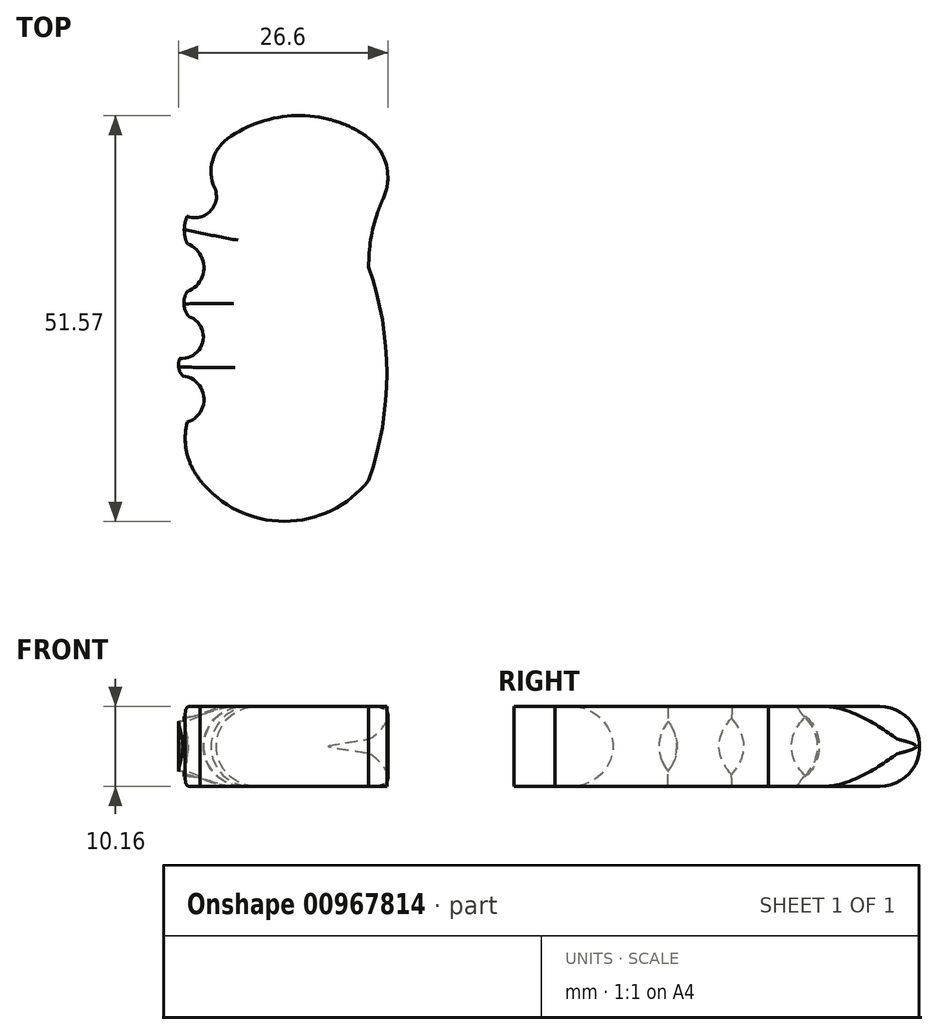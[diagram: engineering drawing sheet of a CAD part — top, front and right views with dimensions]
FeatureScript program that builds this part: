
annotation { "Feature Type Name" : "Feature", "Feature Type Description" : "" }
export const myFeature = defineFeature(function(context is Context, id is Id, definition is map)
    precondition{}
    {
        {
            var Q0;
            Q0=qCreatedBy(makeId("Top.planeOp"),FACE);
            var sketch = newSketch(context, id + "F0", { "sketchPlane" : qUnion([Q0])});
            skArc(sketch, "E0", {"start": v(-14.66, 3.04) * mm, "mid": v(-12.55, 6.22) * mm, "end": v(-15.2, 8.94) * mm});
            skArc(sketch, "E1", {"start": v(-15.58, 11.15) * mm, "mid": v(-12.66, 13.34) * mm, "end": v(-14.47, 16.5) * mm});
            skArc(sketch, "E2", {"start": v(-14.66, 19.63) * mm, "mid": v(-12.52, 22.68) * mm, "end": v(-14.66, 25.72) * mm});
            skArc(sketch, "E3", {"start": v(-14.66, 29.22) * mm, "mid": v(-11.16, 30.67) * mm, "end": v(-12.52, 34.2) * mm});
            skPoint(sketch, "E3.endSnap0", {"position": v(-12.52, 22.68) * mm});
            skArc(sketch, "E4", {"start": v(3.23, 41.57) * mm, "mid": v(-4.58, 41.44) * mm, "end": v(-11.34, 37.52) * mm});
            skArc(sketch, "E5", {"start": v(8.12, 39.35) * mm, "mid": v(5.78, 40.69) * mm, "end": v(3.23, 41.57) * mm});
            skArc(sketch, "E6", {"start": v(10.26, 31.5) * mm, "mid": v(8.84, 27.24) * mm, "end": v(8.4, 22.77) * mm});
            skPoint(sketch, "E6.endSnap0", {"position": v(8.4, 39.15) * mm});
            skArc(sketch, "E7", {"start": v(8.4, -4.33) * mm, "mid": v(10.7, 9.22) * mm, "end": v(8.4, 22.77) * mm});
            skArc(sketch, "E8", {"start": v(-13, -4.33) * mm, "mid": v(-2.3, -9.56) * mm, "end": v(8.4, -4.33) * mm});
            skPoint(sketch, "E9.visualSharp", {"position": v(12.26, 34.94) * mm});
            skArc(sketch, "E9.filletArc", {"start": v(10.26, 31.5) * mm, "mid": v(10.61, 35.8) * mm, "end": v(8.12, 39.35) * mm});
            skArc(sketch, "E10", {"start": v(-14.66, 3.04) * mm, "mid": v(-14.7, -0.84) * mm, "end": v(-13, -4.33) * mm});
            skArc(sketch, "E11", {"start": v(-15.58, 11.15) * mm, "mid": v(-15.74, 9.99) * mm, "end": v(-15.2, 8.94) * mm});
            skArc(sketch, "E12", {"start": v(-14.66, 19.63) * mm, "mid": v(-15.07, 18.04) * mm, "end": v(-14.47, 16.5) * mm});
            skArc(sketch, "E13", {"start": v(-14.66, 29.22) * mm, "mid": v(-15.02, 27.47) * mm, "end": v(-14.66, 25.72) * mm});
            skArc(sketch, "E14", {"start": v(-11.34, 37.52) * mm, "mid": v(-12.25, 35.97) * mm, "end": v(-12.52, 34.2) * mm});
            skSolve(sketch);
        }
        {
            var Q0;
            Q0=qSketchRegion(id+"F0",true);
            extrude(context, id + "F1", {"entities" : qUnion([Q0]), "depth" : 5.08 * mm, "offsetDistance" : 25.4 * mm});
        }
        {
            var Q0;
            Q0=makeQuery(id+"F1.opExtrude","CAP_EDGE",EDGE,{"disambiguationData":[OSD([sQuery(id+"F0.wireOp",EDGE,"E2")])],"isStart":false});
            var Q1;
            Q1=makeQuery(id+"F1.opExtrude","CAP_EDGE",EDGE,{"disambiguationData":[OSD([sQuery(id+"F0.wireOp",EDGE,"E3")])],"isStart":false});
            var Q2;
            Q2=makeQuery(id+"F1.opExtrude","CAP_EDGE",EDGE,{"disambiguationData":[OSD([sQuery(id+"F0.wireOp",EDGE,"E1")])],"isStart":false});
            var Q3;
            Q3=makeQuery(id+"F1.opExtrude","CAP_EDGE",EDGE,{"disambiguationData":[OSD([sQuery(id+"F0.wireOp",EDGE,"E0")])],"isStart":false});
            fillet(context, id + "F2", {"entities" : qUnion([Q0, Q1, Q2, Q3]), "radius" : 5.08 * mm, "tangentPropagation" : true, "allowEdgeOverflow" : false});
        }
        {
            var Q0;
            Q0=makeQuery(id+"F1.opExtrude","SWEPT_BODY",BODY,{"disambiguationData":[OSD([sQuery(id+"F0.wireOp",EDGE,"E0"),sQuery(id+"F0.wireOp",EDGE,"E1"),sQuery(id+"F0.wireOp",EDGE,"E2"),sQuery(id+"F0.wireOp",EDGE,"E3"),sQuery(id+"F0.wireOp",EDGE,"E4"),sQuery(id+"F0.wireOp",EDGE,"E5"),sQuery(id+"F0.wireOp",EDGE,"E6"),sQuery(id+"F0.wireOp",EDGE,"E7"),sQuery(id+"F0.wireOp",EDGE,"E8"),sQuery(id+"F0.wireOp",EDGE,"E9.filletArc"),sQuery(id+"F0.wireOp",EDGE,"E10"),sQuery(id+"F0.wireOp",EDGE,"E11"),sQuery(id+"F0.wireOp",EDGE,"E12"),sQuery(id+"F0.wireOp",EDGE,"E13"),sQuery(id+"F0.wireOp",EDGE,"E14")])]});
            var Q1;
            Q1=qCreatedBy(makeId("Top.planeOp"),FACE);
            mirror(context, id + "F3", {"operationType" : NewBodyOperationType.ADD, "entities" : qUnion([Q0]), "mirrorPlane" : qUnion([Q1])});
        }
        {
            var Q0;
            Q0=makeQuery(id+"F1.opExtrude","CAP_EDGE",EDGE,{"disambiguationData":[OSD([sQuery(id+"F0.wireOp",EDGE,"E4")])],"isStart":false});
            fillet(context, id + "F4", {"entities" : qUnion([Q0]), "radius" : 5.08 * mm, "tangentPropagation" : true, "allowEdgeOverflow" : false});
        }
    });
